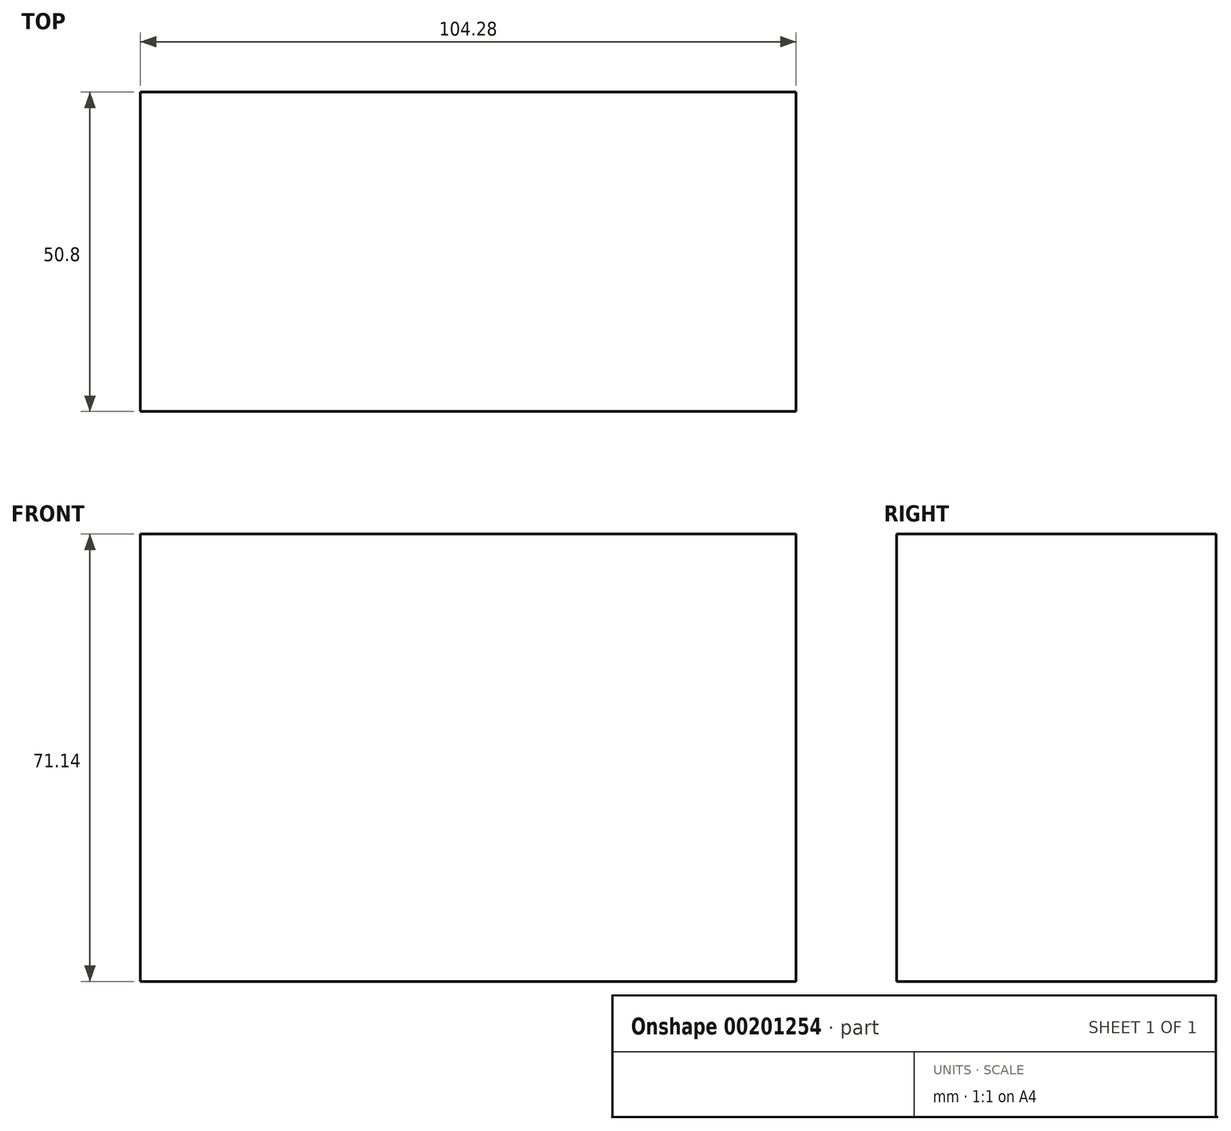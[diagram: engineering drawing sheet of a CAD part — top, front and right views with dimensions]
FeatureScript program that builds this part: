
annotation { "Feature Type Name" : "Feature", "Feature Type Description" : "" }
export const myFeature = defineFeature(function(context is Context, id is Id, definition is map)
    precondition{}
    {
        {
            var Q0;
            Q0=qCreatedBy(makeId("Front.planeOp"),FACE);
            var sketch = newSketch(context, id + "F0", { "sketchPlane" : qUnion([Q0])});
            skLineSegment(sketch, "E0.bottom", {"start": v(52.14, 35.57) * mm, "end": v(-52.14, 35.57) * mm});
            skLineSegment(sketch, "E0.top", {"start": v(52.14, -35.57) * mm, "end": v(-52.14, -35.57) * mm});
            skLineSegment(sketch, "E0.left", {"start": v(52.14, 35.57) * mm, "end": v(52.14, -35.57) * mm});
            skLineSegment(sketch, "E0.right", {"start": v(-52.14, 35.57) * mm, "end": v(-52.14, -35.57) * mm});
            skPoint(sketch, "E0.middle", {"position": v(0, 0) * mm});
            skSolve(sketch);
        }
        {
            var Q0;
            Q0=makeQuery(id+"F0.imprint","IMPRINT",FACE,{"disambiguationData":[TD([[makeQuery(id+"F0.imprint","IMPRINT",EDGE,{"derivedFrom":sQuery(id+"F0.wireOp",EDGE,"E0.bottom")}),1.0]])]});
            extrude(context, id + "F1", {"entities" : qUnion([Q0]), "depth" : 25.4 * mm, "hasSecondDirection" : true, "secondDirectionOppositeDirection" : true, "secondDirectionDepth" : 25.4 * mm});
        }
    });
